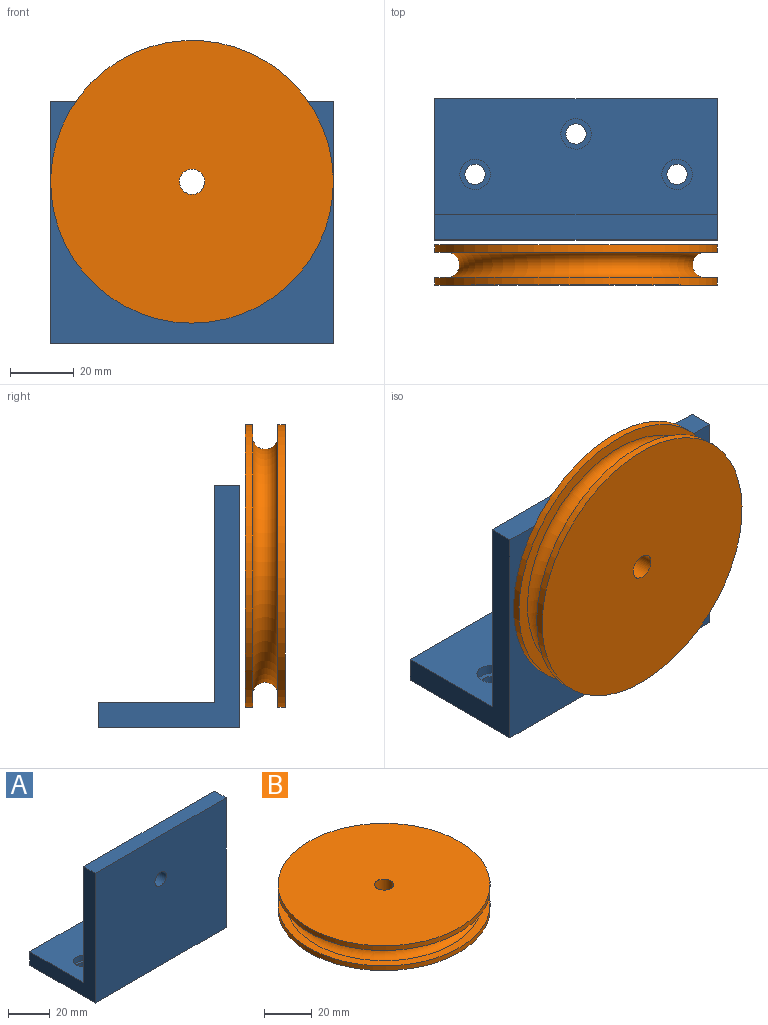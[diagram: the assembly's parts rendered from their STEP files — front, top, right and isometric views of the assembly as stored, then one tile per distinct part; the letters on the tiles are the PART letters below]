
ASSEMBLY  parts=2 mates=1
PART A: 18 faces, bbox 88.9x44.5x76.2 mm
  f0: cylinder r=3.17mm len=6.35mm, axis (0,0,1), area 95mm2, adj f3,f17
  f1: cylinder r=3.17mm len=6.35mm, axis (0,0,1), area 95mm2, adj f3,f15
  f2: cylinder r=3.17mm len=6.35mm, axis (0,0,1), area 95mm2, adj f3,f13
  f3: plane 88.9x44.45mm, normal (0,0,-1), area 3856.6mm2, adj f0,f1,f2,f4,f8,f9,f10
  f4: plane 88.9x7.94mm, normal (0,1,0), area 705.6mm2, adj f3,f5,f9,f10
  f5: plane 88.9x36.51mm, normal (0,0,1), area 3032.2mm2, adj f4,f6,f9,f10,f12,f14,f16
  f6: plane 88.9x68.26mm, normal (0,1,0), area 6019.1mm2, adj f5,f7,f9,f10,f11
  f7: plane 88.9x7.94mm, normal (0,0,1), area 705.6mm2, adj f6,f8,f9,f10
  f8: plane 88.9x76.2mm, normal (0,-1,0), area 6724.7mm2, adj f3,f7,f9,f10,f11
  f9: plane 76.2x44.45mm, normal (-1,0,0), area 894.7mm2, adj f3,f4,f5,f6,f7,f8
  f10: plane 76.2x44.45mm, normal (1,0,0), area 894.7mm2, adj f3,f4,f5,f6,f7,f8
  f11: cylinder r=3.97mm len=7.94mm, axis (0,-1,0), area 197.9mm2, adj f6,f8
  f12: cylinder r=4.76mm len=9.53mm, axis (0,0,1), area 95mm2, adj f5,f13
  f13: plane 9.53x9.53mm, normal (0,0,1), area 39.6mm2, adj f2,f12
  f14: cylinder r=4.76mm len=9.53mm, axis (0,0,1), area 95mm2, adj f5,f15
  f15: plane 9.53x9.53mm, normal (0,0,1), area 39.6mm2, adj f1,f14
  f16: cylinder r=4.76mm len=9.53mm, axis (0,0,1), area 95mm2, adj f5,f17
  f17: plane 9.53x9.53mm, normal (0,0,1), area 39.6mm2, adj f0,f16
PART B: 8 faces, bbox 94.1x94.1x12.7 mm
  f0: cylinder r=44.45mm len=88.9mm, axis (0,0,-1), area 665.1mm2, adj f4,f5
  f1: cylinder r=44.45mm len=88.9mm, axis (0,0,-1), area 665.1mm2, adj f3,f6
  f2: cylinder r=3.97mm len=12.7mm, axis (0,0,-1), area 316.7mm2, adj f3,f4
  f3: plane 88.9x88.9mm, normal (0,0,1), area 6157.7mm2, adj f1,f2
  f4: plane 88.9x88.9mm, normal (0,0,-1), area 6157.7mm2, adj f0,f2
  f5: plane 88.9x88.9mm, normal (0,0,1), area 1018.5mm2, adj f0,f7
  f6: plane 88.9x88.9mm, normal (0,0,-1), area 1018.5mm2, adj f1,f7
  f7: torus R=40.64mm, axis (0,0,1), area 2985.8mm2, adj f5,f6
PLACE A t=(5.41,-4.82,21.82)mm fixed
PLACE B rot(axis=(0.74,-0.47,0.47),106.8deg) t=(-39.04,-6.41,72.62)mm
MATE revolute B.f2 <-> A.f11  axis (0,1,0) through (-39.04,-6.41,72.62)mm
